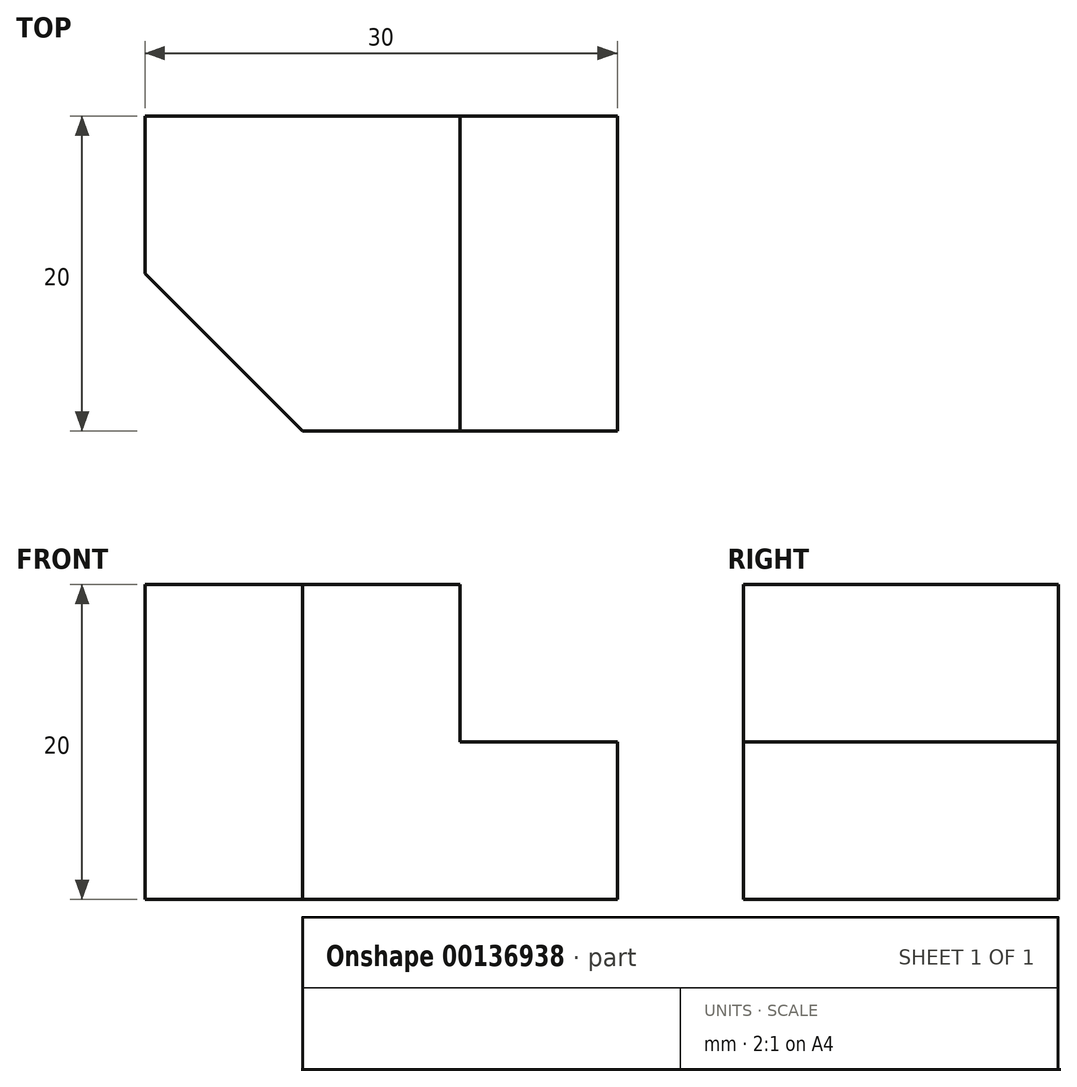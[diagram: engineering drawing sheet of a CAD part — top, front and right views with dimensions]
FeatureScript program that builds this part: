
annotation { "Feature Type Name" : "Feature", "Feature Type Description" : "" }
export const myFeature = defineFeature(function(context is Context, id is Id, definition is map)
    precondition{}
    {
        {
            var Q0;
            Q0=qCreatedBy(makeId("Top.planeOp"),FACE);
            var sketch = newSketch(context, id + "F0", { "sketchPlane" : qUnion([Q0])});
            skLineSegment(sketch, "E0", {"start": v(-20, 10) * mm, "end": v(10, 10) * mm});
            skLineSegment(sketch, "E1", {"start": v(0, 10) * mm, "end": v(0, -10) * mm});
            skLineSegment(sketch, "E2", {"start": v(10, 10) * mm, "end": v(10, -10) * mm});
            skLineSegment(sketch, "E3", {"start": v(10, -10) * mm, "end": v(0, -10) * mm});
            skLineSegment(sketch, "E4", {"start": v(-10, -10) * mm, "end": v(-20, 0) * mm});
            skLineSegment(sketch, "E5", {"start": v(-20, 0) * mm, "end": v(-20, 10) * mm});
            skLineSegment(sketch, "E6", {"start": v(-10, -10) * mm, "end": v(0, -10) * mm});
            skSolve(sketch);
        }
        {
            var Q0;
            Q0 = qSketchRegion(id + "F0", true);
            extrude(context, id + "F1", {"entities" : qUnion([Q0]), "depth" : 20 * mm});
        }
        {
            var Q0;
            Q0=makeQuery(id+"F1.opExtrude","CAP_FACE",FACE,{"disambiguationData":[OSD([sQuery(id+"F0.wireOp",EDGE,"E0"),sQuery(id+"F0.wireOp",EDGE,"E2"),sQuery(id+"F0.wireOp",EDGE,"E3"),sQuery(id+"F0.wireOp",EDGE,"E4"),sQuery(id+"F0.wireOp",EDGE,"E5"),sQuery(id+"F0.wireOp",EDGE,"E6")])],"isStart":false});
            var sketch = newSketch(context, id + "F2", { "sketchPlane" : qUnion([Q0])});
            skLineSegment(sketch, "E7", {"start": v(0, 10) * mm, "end": v(0, -10) * mm});
            skLineSegment(sketch, "E8", {"start": v(0, -10) * mm, "end": v(10, -10) * mm});
            skLineSegment(sketch, "E9", {"start": v(10, -10) * mm, "end": v(10, 10) * mm});
            skLineSegment(sketch, "E10", {"start": v(10, 10) * mm, "end": v(0, 10) * mm});
            skSolve(sketch);
        }
        {
            var Q0;
            Q0=makeQuery(id+"F2.imprint","IMPRINT",FACE,{"disambiguationData":[TD([[makeQuery(id+"F2.imprint","IMPRINT",EDGE,{"derivedFrom":sQuery(id+"F2.wireOp",EDGE,"E7")}),1.0]])]});
            extrude(context, id + "F3", {"entities" : qUnion([Q0]), "operationType" : NewBodyOperationType.REMOVE, "oppositeDirection" : true, "depth" : 10 * mm});
        }
    });
